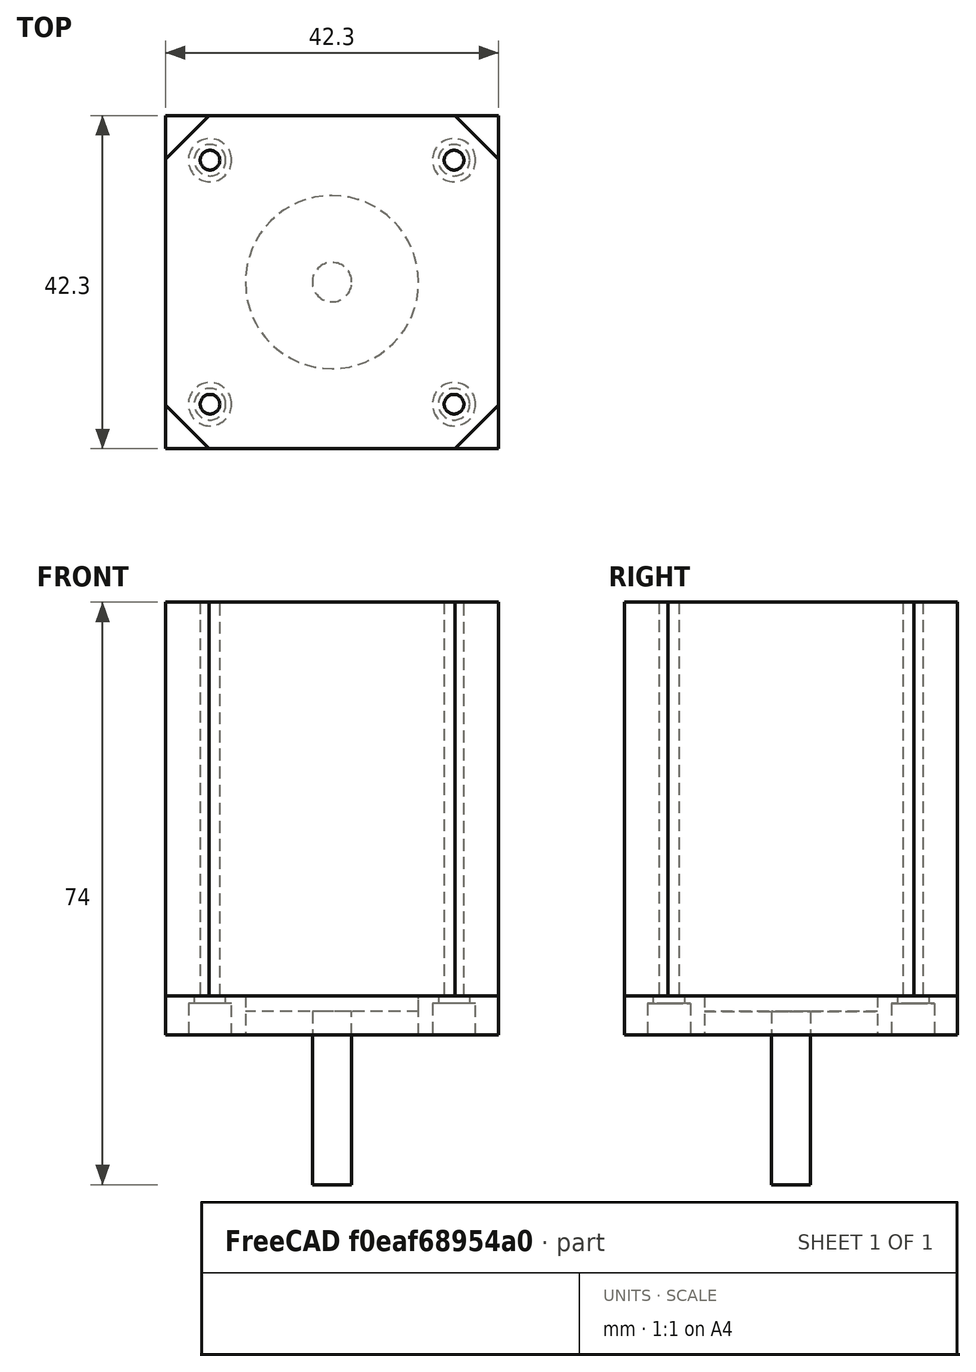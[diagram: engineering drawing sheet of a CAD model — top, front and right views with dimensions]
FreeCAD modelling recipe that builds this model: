
FCSTD DOCUMENT  (FreeCAD 0.21R0.20.1)
Label: NEMA17
License: All rights reserved
LicenseURL: https://en.wikipedia.org/wiki/All_rights_reserved
objects: Part::Cylinder×15, Part::Compound×7, Part::Box×6, Part::MultiFuse×6, Part::Cut×4, Part::Feature×2, Spreadsheet::Sheet×1
note: 40 computed .brp shape members not serialized (recipe doc carries the construction recipe); baked Part::Feature solids carry a one-line shape summary decoded from their .brp

FEATURE [Spreadsheet::Sheet] Spreadsheet  label="NEMA17Parameters"
  cells = A1=Motor length; B1(motorlength)=50; A2=Mountplate thickness; B2(mountplatet)=5; A3=Mountplate below screw; B3(nema17mountplatebelowscrew)=1
FEATURE [Part::Box] Box  label="Cube"
  AttacherType = Attacher::AttachEngine3D
  Height = 50
  Length = 42.3
  Placement = pos=(-21.15,-21.15,0) rot=(0,0,1;0rad)
  Width = 42.3
  expr: Height = <<NEMA17Parameters>>.motorlength
FEATURE [Part::Cylinder] Cylinder
  Angle = 360
  AttacherType = Attacher::AttachEngine3D
  FirstAngle = 0
  Height = 2
  Placement = pos=(0,0,-2) rot=(0,0,1;0rad)
  Radius = 11
  SecondAngle = 0
FEATURE [Part::Cylinder] Cylinder001
  Angle = 360
  AttacherType = Attacher::AttachEngine3D
  FirstAngle = 0
  Height = 24
  Placement = pos=(0,0,-24) rot=(0,0,1;0rad)
  Radius = 2.5
  SecondAngle = 0
FEATURE [Part::Cylinder] Cylinder002
  Angle = 360
  AttacherType = Attacher::AttachEngine3D
  FirstAngle = 0
  Height = 50
  Placement = pos=(15.5,15.5,0) rot=(0,0,1;0rad)
  Radius = 1.25
  SecondAngle = 0
  expr: Height = <<NEMA17Parameters>>.motorlength
FEATURE [Part::Cylinder] Cylinder003
  Angle = 360
  AttacherType = Attacher::AttachEngine3D
  FirstAngle = 0
  Height = 50
  Placement = pos=(-15.5,15.5,0) rot=(0,0,1;0rad)
  Radius = 1.25
  SecondAngle = 0
  expr: Height = <<NEMA17Parameters>>.motorlength
FEATURE [Part::Cylinder] Cylinder004
  Angle = 360
  AttacherType = Attacher::AttachEngine3D
  FirstAngle = 0
  Height = 50
  Placement = pos=(15.5,-15.5,0) rot=(0,0,1;0rad)
  Radius = 1.25
  SecondAngle = 0
  expr: Height = <<NEMA17Parameters>>.motorlength
FEATURE [Part::Cylinder] Cylinder005
  Angle = 360
  AttacherType = Attacher::AttachEngine3D
  FirstAngle = 0
  Height = 50
  Placement = pos=(-15.5,-15.5,0) rot=(0,0,1;0rad)
  Radius = 1.25
  SecondAngle = 0
  expr: Height = <<NEMA17Parameters>>.motorlength
FEATURE [Part::Compound] Compound
  Links = -> [Cylinder005,Cylinder002,Cylinder003,Cylinder004]
FEATURE [Part::MultiFuse] Fusion
  Shapes = -> [Cylinder,Box]
FEATURE [Part::MultiFuse] Fusion001
  Shapes = -> [Cylinder001,Fusion]
FEATURE [Part::Cut] Cut
  Base = -> Fusion001
  Tool = -> Compound
FEATURE [Part::Box] Box001  label="Cube001"
  AttacherType = Attacher::AttachEngine3D
  Height = 50
  Length = 100
  Placement = pos=(26,-50,0) rot=(0,0,1;0rad)
  Width = 100
  expr: Height = <<NEMA17Parameters>>.motorlength
FEATURE [Part::Compound] Compound001
  Links = -> [Box001]
  Placement = pos=(0,0,0) rot=(0,0,1;0.785398rad)
FEATURE [Part::Box] Box002  label="Cube002"
  AttacherType = Attacher::AttachEngine3D
  Height = 50
  Length = 100
  Placement = pos=(26,-50,0) rot=(0,0,1;0rad)
  Width = 100
  expr: Height = <<NEMA17Parameters>>.motorlength
FEATURE [Part::Compound] Compound002
  Links = -> [Box002]
  Placement = pos=(0,0,0) rot=(0,0,1;2.35619rad)
FEATURE [Part::Box] Box003  label="Cube003"
  AttacherType = Attacher::AttachEngine3D
  Height = 50
  Length = 100
  Placement = pos=(26,-50,0) rot=(0,0,1;0rad)
  Width = 100
  expr: Height = <<NEMA17Parameters>>.motorlength
FEATURE [Part::Compound] Compound003
  Links = -> [Box003]
  Placement = pos=(0,0,0) rot=(0,0,1;3.92699rad)
FEATURE [Part::Box] Box004  label="Cube004"
  AttacherType = Attacher::AttachEngine3D
  Height = 50
  Length = 100
  Placement = pos=(26,-50,0) rot=(0,0,1;0rad)
  Width = 100
  expr: Height = <<NEMA17Parameters>>.motorlength
FEATURE [Part::Compound] Compound004
  Links = -> [Box004]
  Placement = pos=(0,0,0) rot=(0,0,1;5.49779rad)
FEATURE [Part::Compound] Compound005
  Links = -> [Compound001,Compound002,Compound003,Compound004]
FEATURE [Part::Cut] Cut001
  Base = -> Cut
  Tool = -> Compound005
FEATURE [Part::Feature] Cut001_solid  label="MotorTemplate"
  shape: bbox 42.3 x 42.3 x 74 mm, 18 faces (baked)
FEATURE [Part::Box] Box005  label="Cube005"
  AttacherType = Attacher::AttachEngine3D
  Height = 5
  Length = 42.3
  Placement = pos=(-21.15,-21.15,-5) rot=(0,0,1;0rad)
  Width = 42.3
  expr: .Placement.Base.z = -<<NEMA17Parameters>>.mountplatet
  expr: Height = <<NEMA17Parameters>>.mountplatet
FEATURE [Part::Cylinder] Cylinder006
  Angle = 360
  AttacherType = Attacher::AttachEngine3D
  FirstAngle = 0
  Height = 5
  Placement = pos=(0,0,-5) rot=(0,0,1;0rad)
  Radius = 11
  SecondAngle = 0
  expr: .Placement.Base.z = -<<NEMA17Parameters>>.mountplatet
  expr: Height = <<NEMA17Parameters>>.mountplatet
FEATURE [Part::Cut] Cut002
  Base = -> Box005
  Tool = -> Cylinder006
FEATURE [Part::Cylinder] Cylinder007
  Angle = 360
  AttacherType = Attacher::AttachEngine3D
  FirstAngle = 0
  Height = 4
  Placement = pos=(0,0,-5) rot=(0,0,1;0rad)
  Radius = 2.75
  SecondAngle = 0
  expr: .Placement.Base.z = -<<NEMA17Parameters>>.mountplatet
  expr: Height = <<NEMA17Parameters>>.mountplatet - <<NEMA17Parameters>>.nema17mountplatebelowscrew
FEATURE [Part::Cylinder] Cylinder008
  Angle = 360
  AttacherType = Attacher::AttachEngine3D
  FirstAngle = 0
  Height = 5
  Placement = pos=(0,0,-5) rot=(0,0,1;0rad)
  Radius = 2
  SecondAngle = 0
  expr: .Placement.Base.z = -<<NEMA17Parameters>>.mountplatet
  expr: Height = <<NEMA17Parameters>>.mountplatet
FEATURE [Part::MultiFuse] Fusion002
  Placement = pos=(-15.5,-15.5,0) rot=(0,0,1;0rad)
  Shapes = -> [Cylinder007,Cylinder008]
FEATURE [Part::Cylinder] Cylinder009
  Angle = 360
  AttacherType = Attacher::AttachEngine3D
  FirstAngle = 0
  Height = 4
  Placement = pos=(0,0,-5) rot=(0,0,1;0rad)
  Radius = 2.75
  SecondAngle = 0
  expr: .Placement.Base.z = -<<NEMA17Parameters>>.mountplatet
  expr: Height = <<NEMA17Parameters>>.mountplatet - <<NEMA17Parameters>>.nema17mountplatebelowscrew
FEATURE [Part::Cylinder] Cylinder010
  Angle = 360
  AttacherType = Attacher::AttachEngine3D
  FirstAngle = 0
  Height = 5
  Placement = pos=(0,0,-5) rot=(0,0,1;0rad)
  Radius = 2
  SecondAngle = 0
  expr: .Placement.Base.z = -<<NEMA17Parameters>>.mountplatet
  expr: Height = <<NEMA17Parameters>>.mountplatet
FEATURE [Part::MultiFuse] Fusion003
  Placement = pos=(15.5,-15.5,0) rot=(0,0,1;0rad)
  Shapes = -> [Cylinder009,Cylinder010]
FEATURE [Part::Cylinder] Cylinder011
  Angle = 360
  AttacherType = Attacher::AttachEngine3D
  FirstAngle = 0
  Height = 4
  Placement = pos=(0,0,-5) rot=(0,0,1;0rad)
  Radius = 2.75
  SecondAngle = 0
  expr: .Placement.Base.z = -<<NEMA17Parameters>>.mountplatet
  expr: Height = <<NEMA17Parameters>>.mountplatet - <<NEMA17Parameters>>.nema17mountplatebelowscrew
FEATURE [Part::Cylinder] Cylinder012
  Angle = 360
  AttacherType = Attacher::AttachEngine3D
  FirstAngle = 0
  Height = 5
  Placement = pos=(0,0,-5) rot=(0,0,1;0rad)
  Radius = 2
  SecondAngle = 0
  expr: .Placement.Base.z = -<<NEMA17Parameters>>.mountplatet
  expr: Height = <<NEMA17Parameters>>.mountplatet
FEATURE [Part::MultiFuse] Fusion004
  Placement = pos=(-15.5,15.5,0) rot=(0,0,1;0rad)
  Shapes = -> [Cylinder011,Cylinder012]
FEATURE [Part::Cylinder] Cylinder013
  Angle = 360
  AttacherType = Attacher::AttachEngine3D
  FirstAngle = 0
  Height = 4
  Placement = pos=(0,0,-5) rot=(0,0,1;0rad)
  Radius = 2.75
  SecondAngle = 0
  expr: .Placement.Base.z = -<<NEMA17Parameters>>.mountplatet
  expr: Height = <<NEMA17Parameters>>.mountplatet - <<NEMA17Parameters>>.nema17mountplatebelowscrew
FEATURE [Part::Cylinder] Cylinder014
  Angle = 360
  AttacherType = Attacher::AttachEngine3D
  FirstAngle = 0
  Height = 5
  Placement = pos=(0,0,-5) rot=(0,0,1;0rad)
  Radius = 2
  SecondAngle = 0
  expr: .Placement.Base.z = -<<NEMA17Parameters>>.mountplatet
  expr: Height = <<NEMA17Parameters>>.mountplatet
FEATURE [Part::MultiFuse] Fusion005
  Placement = pos=(15.5,15.5,0) rot=(0,0,1;0rad)
  Shapes = -> [Cylinder013,Cylinder014]
FEATURE [Part::Compound] Compound006
  Links = -> [Fusion005,Fusion004,Fusion003,Fusion002]
FEATURE [Part::Cut] Cut003
  Base = -> Cut002
  Tool = -> Compound006
FEATURE [Part::Feature] Cut003_solid  label="MountplateTemplate"
  shape: bbox 42.3 x 42.3 x 5 mm, 19 faces (baked)
